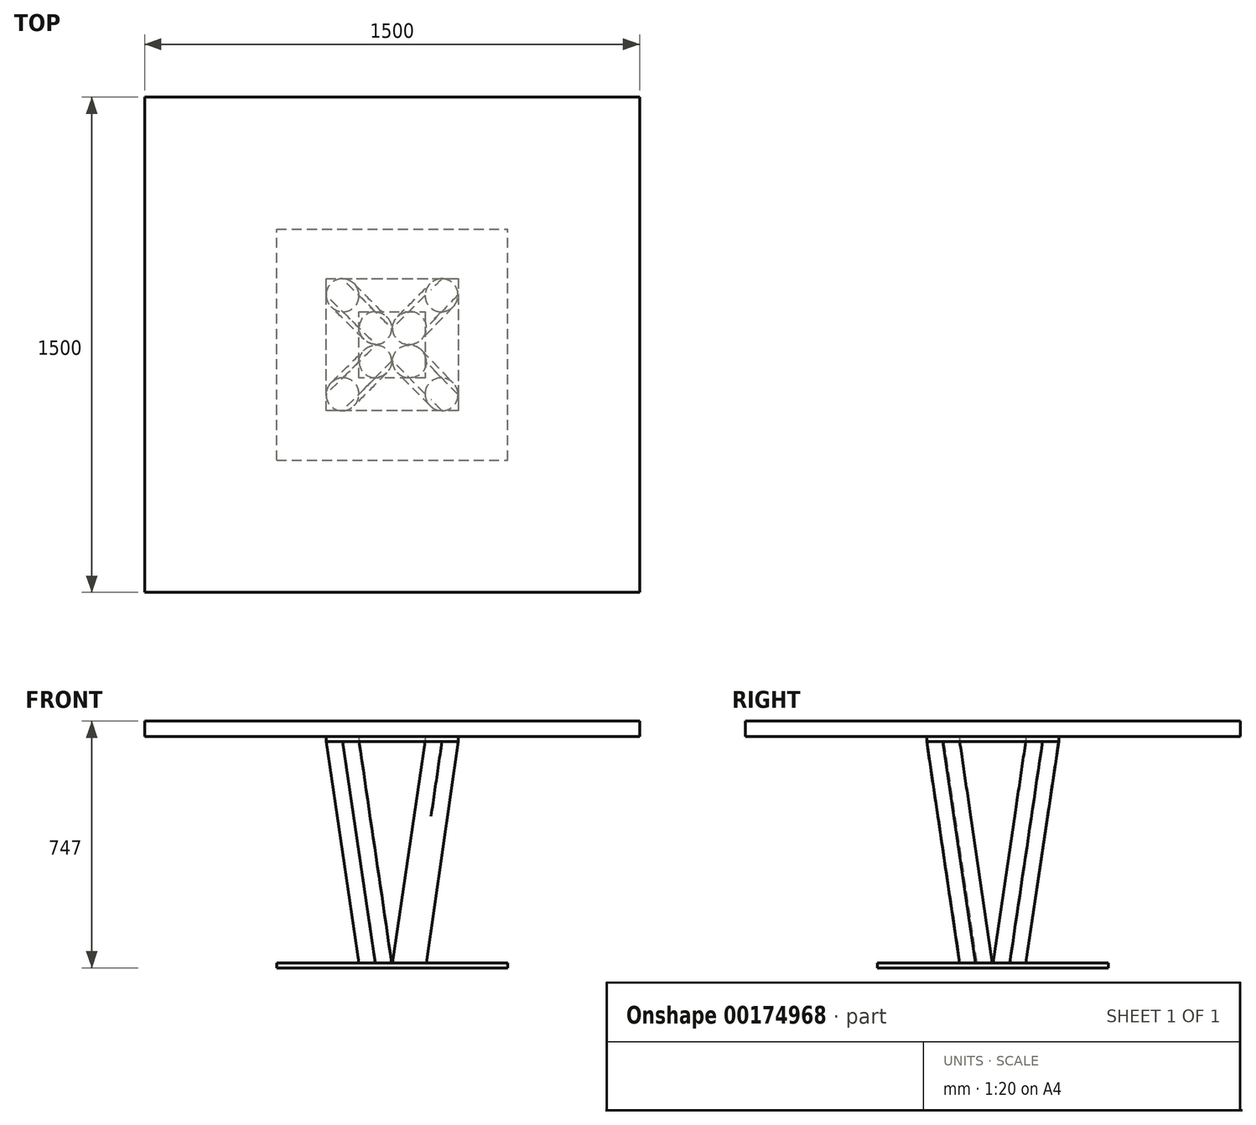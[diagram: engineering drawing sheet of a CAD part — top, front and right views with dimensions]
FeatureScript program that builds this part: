
annotation { "Feature Type Name" : "Feature", "Feature Type Description" : "" }
export const myFeature = defineFeature(function(context is Context, id is Id, definition is map)
    precondition{}
    {
        {
            var Q0;
            Q0=qCreatedBy(makeId("Front.planeOp"),FACE);
            var sketch = newSketch(context, id + "F0", { "sketchPlane" : qUnion([Q0])});
            skLineSegment(sketch, "E0.bottom", {"start": v(-350, -7.5) * mm, "end": v(350, -7.5) * mm});
            skLineSegment(sketch, "E0.top", {"start": v(-350, 7.5) * mm, "end": v(350, 7.5) * mm});
            skLineSegment(sketch, "E0.left", {"start": v(-350, -7.5) * mm, "end": v(-350, 7.5) * mm});
            skLineSegment(sketch, "E0.right", {"start": v(350, -7.5) * mm, "end": v(350, 7.5) * mm});
            skPoint(sketch, "E0.middle", {"position": v(0, 0) * mm});
            skSolve(sketch);
        }
        {
            var Q0;
            Q0 = qSketchRegion(id + "F0", true);
            extrude(context, id + "F1", {"entities" : qUnion([Q0]), "endBound" : BoundingType.SYMMETRIC, "depth" : 700 * mm});
        }
        {
            var Q0;
            Q0=makeQuery(id+"F1.opExtrude","SWEPT_FACE",FACE,{"disambiguationData":[OSD([sQuery(id+"F0.wireOp",EDGE,"E0.top")])]});
            var sketch = newSketch(context, id + "F2", { "sketchPlane" : qUnion([Q0])});
            skLineSegment(sketch, "E1.bottom", {"start": v(200, -200) * mm, "end": v(-200, -200) * mm});
            skLineSegment(sketch, "E1.top", {"start": v(200, 200) * mm, "end": v(-200, 200) * mm});
            skLineSegment(sketch, "E1.left", {"start": v(200, -200) * mm, "end": v(200, 200) * mm});
            skLineSegment(sketch, "E1.right", {"start": v(-200, -200) * mm, "end": v(-200, 200) * mm});
            skPoint(sketch, "E1.middle", {"position": v(0, 0) * mm});
            skSolve(sketch);
        }
        {
            var Q0;
            Q0=makeQuery(id+"F2.imprint","IMPRINT",FACE,{"disambiguationData":[TD([[makeQuery(id+"F2.imprint","IMPRINT",EDGE,{"derivedFrom":sQuery(id+"F2.wireOp",EDGE,"E1.bottom")}),-1.0]])]});
            extrude(context, id + "F3", {"entities" : qUnion([Q0]), "operationType" : NewBodyOperationType.ADD, "depth" : 670 * mm});
        }
        {
            var Q0;
            Q0=makeQuery(id+"F3.opExtrude","SWEPT_FACE",FACE,{"disambiguationData":[OSD([sQuery(id+"F2.wireOp",EDGE,"E1.right")])]});
            var sketch = newSketch(context, id + "F4", { "sketchPlane" : qUnion([Q0])});
            skLineSegment(sketch, "E2", {"start": v(200, 7.5) * mm, "end": v(200, 677.5) * mm});
            skLineSegment(sketch, "E3", {"start": v(200, 677.5) * mm, "end": v(100, 7.5) * mm});
            skLineSegment(sketch, "E4", {"start": v(100, 7.5) * mm, "end": v(200, 7.5) * mm});
            skLineSegment(sketch, "E5.MirrorCS", {"start": v(-200, 7.5) * mm, "end": v(-200, 677.5) * mm});
            skLineSegment(sketch, "E6.MirrorCS", {"start": v(-200, 677.5) * mm, "end": v(-100, 7.5) * mm});
            skLineSegment(sketch, "E7.MirrorCS", {"start": v(-100, 7.5) * mm, "end": v(-200, 7.5) * mm});
            skLineSegment(sketch, "E8", {"start": v(0, 0) * mm, "end": v(100, 677.5) * mm});
            skLineSegment(sketch, "E9", {"start": v(100, 677.5) * mm, "end": v(-100, 677.5) * mm});
            skLineSegment(sketch, "E10", {"start": v(-100, 677.5) * mm, "end": v(0, 0) * mm});
            skSolve(sketch);
        }
        {
            var Q0;
            Q0=makeQuery(id+"F3.opExtrude","SWEPT_FACE",FACE,{"disambiguationData":[OSD([sQuery(id+"F2.wireOp",EDGE,"E1.top")])]});
            var sketch = newSketch(context, id + "F5", { "sketchPlane" : qUnion([Q0])});
            skLineSegment(sketch, "E11", {"start": v(200, 7.5) * mm, "end": v(200, 677.5) * mm});
            skLineSegment(sketch, "E12", {"start": v(200, 677.5) * mm, "end": v(100, 7.5) * mm});
            skLineSegment(sketch, "E13", {"start": v(100, 7.5) * mm, "end": v(200, 7.5) * mm});
            skLineSegment(sketch, "E14.MirrorCS", {"start": v(-104.26, 7.5) * mm, "end": v(-200, 7.5) * mm});
            skLineSegment(sketch, "E15.MirrorCS", {"start": v(-100, 7.5) * mm, "end": v(-200, 7.5) * mm});
            skLineSegment(sketch, "E16.MirrorCS", {"start": v(-200, 677.5) * mm, "end": v(-104.26, 7.5) * mm});
            skLineSegment(sketch, "E17.MirrorCS", {"start": v(-200, 7.5) * mm, "end": v(-200, 677.5) * mm});
            skLineSegment(sketch, "E18", {"start": v(0, 0) * mm, "end": v(100, 677.5) * mm});
            skLineSegment(sketch, "E19", {"start": v(100, 677.5) * mm, "end": v(-100, 677.5) * mm});
            skLineSegment(sketch, "E20", {"start": v(-100, 677.5) * mm, "end": v(0, 0) * mm});
            skSolve(sketch);
        }
        {
            var Q0;
            Q0=makeQuery(id+"F5.imprint","IMPRINT",FACE,{"disambiguationData":[TD([[makeQuery(id+"F5.imprint","IMPRINT",EDGE,{"derivedFrom":sQuery(id+"F5.wireOp",EDGE,"E11")}),-1.0]])]});
            var Q1;
            {var subQ2=sQuery(id+"F5.wireOp",EDGE,"E16.MirrorCS");Q1=makeQuery(id+"F5.imprint","IMPRINT",FACE,{"disambiguationData":[TD([[makeQuery(id+"F5.imprint","IMPRINT",EDGE,{"derivedFrom":subQ2}),-1.0]])]});}
            extrude(context, id + "F6", {"entities" : qUnion([Q0, Q1]), "operationType" : NewBodyOperationType.REMOVE, "oppositeDirection" : true, "depth" : 2934.37 * mm});
        }
        {
            var Q0;
            Q0=makeQuery(id+"F4.imprint","IMPRINT",FACE,{"disambiguationData":[TD([[makeQuery(id+"F4.imprint","IMPRINT",EDGE,{"derivedFrom":sQuery(id+"F4.wireOp",EDGE,"E2")}),-1.0]])]});
            var Q1;
            Q1=makeQuery(id+"F4.imprint","IMPRINT",FACE,{"disambiguationData":[TD([[makeQuery(id+"F4.imprint","IMPRINT",EDGE,{"derivedFrom":sQuery(id+"F4.wireOp",EDGE,"E5.MirrorCS")}),1.0]])]});
            extrude(context, id + "F7", {"entities" : qUnion([Q0, Q1]), "operationType" : NewBodyOperationType.REMOVE, "oppositeDirection" : true, "depth" : 1558.7 * mm});
        }
        {
            var Q0;
            {var subQ0=sQuery(id+"F4.wireOp",EDGE,"E9");Q0=makeQuery(id+"F4.imprint","IMPRINT",FACE,{"disambiguationData":[TD([[makeQuery(id+"F4.imprint","IMPRINT",EDGE,{"derivedFrom":subQ0}),1.0]])]});}
            extrude(context, id + "F8", {"entities" : qUnion([Q0]), "operationType" : NewBodyOperationType.REMOVE, "oppositeDirection" : true, "depth" : 2927.5 * mm});
        }
        {
            var Q0;
            {var subQ0=sQuery(id+"F5.wireOp",EDGE,"E19");Q0=makeQuery(id+"F5.imprint","IMPRINT",FACE,{"disambiguationData":[TD([[makeQuery(id+"F5.imprint","IMPRINT",EDGE,{"derivedFrom":subQ0}),-1.0]])]});}
            extrude(context, id + "F9", {"entities" : qUnion([Q0]), "operationType" : NewBodyOperationType.REMOVE, "oppositeDirection" : true, "depth" : 814.42 * mm});
        }
        {
            var Q0;
            Q0=makeQuery(id+"F7.boolean.opBoolean","INTERSECT",EDGE,{"derivedFrom":[makeQuery(id+"F6.boolean.opBoolean","COPY",FACE,{"derivedFrom":makeQuery(id+"F6.opExtrude","SWEPT_FACE",FACE,{"disambiguationData":[OSD([sQuery(id+"F5.wireOp",EDGE,"E12")])]})}),makeQuery(id+"F7.opExtrude","SWEPT_FACE",FACE,{"disambiguationData":[OSD([sQuery(id+"F4.wireOp",EDGE,"E3")])]})]});
            fillet(context, id + "F10", {"entities" : qUnion([Q0]), "radius" : 50 * mm, "tangentPropagation" : true, "allowEdgeOverflow" : false});
        }
        {
            var Q0;
            Q0=makeQuery(id+"F8.boolean.opBoolean","INTERSECT",EDGE,{"derivedFrom":[makeQuery(id+"F6.boolean.opBoolean","COPY",FACE,{"derivedFrom":makeQuery(id+"F6.opExtrude","SWEPT_FACE",FACE,{"disambiguationData":[OSD([sQuery(id+"F5.wireOp",EDGE,"E12")])]})}),makeQuery(id+"F8.opExtrude","SWEPT_FACE",FACE,{"disambiguationData":[OSD([sQuery(id+"F4.wireOp",EDGE,"E8")])]})]});
            fillet(context, id + "F11", {"entities" : qUnion([Q0]), "radius" : 50 * mm, "tangentPropagation" : true, "allowEdgeOverflow" : false});
        }
        {
            var Q0;
            Q0=makeQuery(id+"F7.boolean.opBoolean","INTERSECT",EDGE,{"derivedFrom":[makeQuery(id+"F6.boolean.opBoolean","COPY",FACE,{"derivedFrom":makeQuery(id+"F6.opExtrude","SWEPT_FACE",FACE,{"disambiguationData":[OSD([sQuery(id+"F5.wireOp",EDGE,"E12")])]})}),makeQuery(id+"F7.opExtrude","SWEPT_FACE",FACE,{"disambiguationData":[OSD([sQuery(id+"F4.wireOp",EDGE,"E6.MirrorCS")])]})]});
            fillet(context, id + "F12", {"entities" : qUnion([Q0]), "radius" : 50 * mm, "tangentPropagation" : true, "allowEdgeOverflow" : false});
        }
        {
            var Q0;
            Q0=makeQuery(id+"F9.boolean.opBoolean","INTERSECT",EDGE,{"derivedFrom":[makeQuery(id+"F7.boolean.opBoolean","COPY",FACE,{"derivedFrom":makeQuery(id+"F7.opExtrude","SWEPT_FACE",FACE,{"disambiguationData":[OSD([sQuery(id+"F4.wireOp",EDGE,"E6.MirrorCS")])]})}),makeQuery(id+"F9.opExtrude","SWEPT_FACE",FACE,{"disambiguationData":[OSD([sQuery(id+"F5.wireOp",EDGE,"E18")])]})]});
            fillet(context, id + "F13", {"entities" : qUnion([Q0]), "radius" : 50 * mm, "tangentPropagation" : true, "allowEdgeOverflow" : false});
        }
        {
            var Q0;
            Q0=makeQuery(id+"F8.boolean.opBoolean","INTERSECT",EDGE,{"derivedFrom":[makeQuery(id+"F6.boolean.opBoolean","COPY",FACE,{"derivedFrom":makeQuery(id+"F6.opExtrude","SWEPT_FACE",FACE,{"disambiguationData":[OSD([sQuery(id+"F5.wireOp",EDGE,"E16.MirrorCS")])]})}),makeQuery(id+"F8.opExtrude","SWEPT_FACE",FACE,{"disambiguationData":[OSD([sQuery(id+"F4.wireOp",EDGE,"E10")])]})]});
            var Q1;
            Q1=makeQuery(id+"F7.boolean.opBoolean","INTERSECT",EDGE,{"derivedFrom":[makeQuery(id+"F6.boolean.opBoolean","COPY",FACE,{"derivedFrom":makeQuery(id+"F6.opExtrude","SWEPT_FACE",FACE,{"disambiguationData":[OSD([sQuery(id+"F5.wireOp",EDGE,"E16.MirrorCS")])]})}),makeQuery(id+"F7.opExtrude","SWEPT_FACE",FACE,{"disambiguationData":[OSD([sQuery(id+"F4.wireOp",EDGE,"E6.MirrorCS")])]})]});
            fillet(context, id + "F14", {"entities" : qUnion([Q0, Q1]), "radius" : 50 * mm, "tangentPropagation" : true, "allowEdgeOverflow" : false});
        }
        {
            var Q0;
            Q0=makeQuery(id+"F9.boolean.opBoolean","INTERSECT",EDGE,{"derivedFrom":[makeQuery(id+"F8.boolean.opBoolean","COPY",FACE,{"derivedFrom":makeQuery(id+"F8.opExtrude","SWEPT_FACE",FACE,{"disambiguationData":[OSD([sQuery(id+"F4.wireOp",EDGE,"E10")])]})}),makeQuery(id+"F9.opExtrude","SWEPT_FACE",FACE,{"disambiguationData":[OSD([sQuery(id+"F5.wireOp",EDGE,"E18")])]})]});
            var Q1;
            Q1=makeQuery(id+"F8.boolean.opBoolean","INTERSECT",EDGE,{"derivedFrom":[makeQuery(id+"F6.boolean.opBoolean","COPY",FACE,{"derivedFrom":makeQuery(id+"F6.opExtrude","SWEPT_FACE",FACE,{"disambiguationData":[OSD([sQuery(id+"F5.wireOp",EDGE,"E16.MirrorCS")])]})}),makeQuery(id+"F8.opExtrude","SWEPT_FACE",FACE,{"disambiguationData":[OSD([sQuery(id+"F4.wireOp",EDGE,"E8")])]})]});
            var Q2;
            Q2=makeQuery(id+"F9.boolean.opBoolean","INTERSECT",EDGE,{"derivedFrom":[makeQuery(id+"F7.boolean.opBoolean","COPY",FACE,{"derivedFrom":makeQuery(id+"F7.opExtrude","SWEPT_FACE",FACE,{"disambiguationData":[OSD([sQuery(id+"F4.wireOp",EDGE,"E3")])]})}),makeQuery(id+"F9.opExtrude","SWEPT_FACE",FACE,{"disambiguationData":[OSD([sQuery(id+"F5.wireOp",EDGE,"E18")])]})]});
            fillet(context, id + "F15", {"entities" : qUnion([Q0, Q1, Q2]), "radius" : 50 * mm, "tangentPropagation" : true, "allowEdgeOverflow" : false});
        }
        {
            var Q0;
            Q0=makeQuery(id+"F7.boolean.opBoolean","INTERSECT",EDGE,{"derivedFrom":[makeQuery(id+"F6.boolean.opBoolean","COPY",FACE,{"derivedFrom":makeQuery(id+"F6.opExtrude","SWEPT_FACE",FACE,{"disambiguationData":[OSD([sQuery(id+"F5.wireOp",EDGE,"E16.MirrorCS")])]})}),makeQuery(id+"F7.opExtrude","SWEPT_FACE",FACE,{"disambiguationData":[OSD([sQuery(id+"F4.wireOp",EDGE,"E3")])]})]});
            var Q1;
            Q1=makeQuery(id+"F9.boolean.opBoolean","INTERSECT",EDGE,{"derivedFrom":[makeQuery(id+"F7.boolean.opBoolean","COPY",FACE,{"derivedFrom":makeQuery(id+"F7.opExtrude","SWEPT_FACE",FACE,{"disambiguationData":[OSD([sQuery(id+"F4.wireOp",EDGE,"E3")])]})}),makeQuery(id+"F9.opExtrude","SWEPT_FACE",FACE,{"disambiguationData":[OSD([sQuery(id+"F5.wireOp",EDGE,"E20")])]})]});
            fillet(context, id + "F16", {"entities" : qUnion([Q0, Q1]), "radius" : 50 * mm, "tangentPropagation" : true, "allowEdgeOverflow" : false});
        }
        {
            var Q0;
            Q0=makeQuery(id+"F9.boolean.opBoolean","INTERSECT",EDGE,{"derivedFrom":[makeQuery(id+"F8.boolean.opBoolean","COPY",FACE,{"derivedFrom":makeQuery(id+"F8.opExtrude","SWEPT_FACE",FACE,{"disambiguationData":[OSD([sQuery(id+"F4.wireOp",EDGE,"E8")])]})}),makeQuery(id+"F9.opExtrude","SWEPT_FACE",FACE,{"disambiguationData":[OSD([sQuery(id+"F5.wireOp",EDGE,"E18")])]})]});
            fillet(context, id + "F17", {"entities" : qUnion([Q0]), "radius" : 50 * mm, "tangentPropagation" : true, "allowEdgeOverflow" : false});
        }
        {
            var Q0;
            Q0=makeQuery(id+"F9.boolean.opBoolean","INTERSECT",EDGE,{"derivedFrom":[makeQuery(id+"F8.boolean.opBoolean","COPY",FACE,{"derivedFrom":makeQuery(id+"F8.opExtrude","SWEPT_FACE",FACE,{"disambiguationData":[OSD([sQuery(id+"F4.wireOp",EDGE,"E8")])]})}),makeQuery(id+"F9.opExtrude","SWEPT_FACE",FACE,{"disambiguationData":[OSD([sQuery(id+"F5.wireOp",EDGE,"E20")])]})]});
            var Q1;
            Q1=makeQuery(id+"F8.boolean.opBoolean","INTERSECT",EDGE,{"derivedFrom":[makeQuery(id+"F6.boolean.opBoolean","COPY",FACE,{"derivedFrom":makeQuery(id+"F6.opExtrude","SWEPT_FACE",FACE,{"disambiguationData":[OSD([sQuery(id+"F5.wireOp",EDGE,"E12")])]})}),makeQuery(id+"F8.opExtrude","SWEPT_FACE",FACE,{"disambiguationData":[OSD([sQuery(id+"F4.wireOp",EDGE,"E10")])]})]});
            var Q2;
            Q2=makeQuery(id+"F9.boolean.opBoolean","INTERSECT",EDGE,{"derivedFrom":[makeQuery(id+"F8.boolean.opBoolean","COPY",FACE,{"derivedFrom":makeQuery(id+"F8.opExtrude","SWEPT_FACE",FACE,{"disambiguationData":[OSD([sQuery(id+"F4.wireOp",EDGE,"E10")])]})}),makeQuery(id+"F9.opExtrude","SWEPT_FACE",FACE,{"disambiguationData":[OSD([sQuery(id+"F5.wireOp",EDGE,"E20")])]})]});
            fillet(context, id + "F18", {"entities" : qUnion([Q0, Q1, Q2]), "radius" : 50 * mm, "tangentPropagation" : true, "allowEdgeOverflow" : false});
        }
        {
            var Q0;
            Q0=makeQuery(id+"F9.boolean.opBoolean","INTERSECT",EDGE,{"derivedFrom":[makeQuery(id+"F7.boolean.opBoolean","COPY",FACE,{"derivedFrom":makeQuery(id+"F7.opExtrude","SWEPT_FACE",FACE,{"disambiguationData":[OSD([sQuery(id+"F4.wireOp",EDGE,"E6.MirrorCS")])]})}),makeQuery(id+"F9.opExtrude","SWEPT_FACE",FACE,{"disambiguationData":[OSD([sQuery(id+"F5.wireOp",EDGE,"E20")])]})]});
            fillet(context, id + "F19", {"entities" : qUnion([Q0]), "radius" : 50 * mm, "tangentPropagation" : true, "allowEdgeOverflow" : false});
        }
        {
            var Q0;
            {var subQ0=makeQuery(id+"F6.boolean.opBoolean","COPY",FACE,{"derivedFrom":makeQuery(id+"F6.opExtrude","SWEPT_FACE",FACE,{"disambiguationData":[OSD([sQuery(id+"F5.wireOp",EDGE,"E16.MirrorCS")])]})});var subQ1=makeQuery(id+"F7.boolean.opBoolean","COPY",FACE,{"derivedFrom":makeQuery(id+"F7.opExtrude","SWEPT_FACE",FACE,{"disambiguationData":[OSD([sQuery(id+"F4.wireOp",EDGE,"E6.MirrorCS")])]})});Q0=makeQuery(id+"F9.boolean.opBoolean","SPLIT",FACE,{"disambiguationData":[TD([subQ0])],"derivedFrom":makeQuery(id+"F8.boolean.opBoolean","SPLIT",FACE,{"disambiguationData":[TD([subQ1])],"derivedFrom":makeQuery(id+"F3.opExtrude","CAP_FACE",FACE,{"disambiguationData":[OSD([sQuery(id+"F2.wireOp",EDGE,"E1.bottom"),sQuery(id+"F2.wireOp",EDGE,"E1.top"),sQuery(id+"F2.wireOp",EDGE,"E1.left"),sQuery(id+"F2.wireOp",EDGE,"E1.right")])],"isStart":false})})});}
            var sketch = newSketch(context, id + "F20", { "sketchPlane" : qUnion([Q0])});
            skLineSegment(sketch, "E21", {"start": v(200, 200) * mm, "end": v(200, -200) * mm});
            skLineSegment(sketch, "E22", {"start": v(200, -200) * mm, "end": v(-200, -200) * mm});
            skLineSegment(sketch, "E23", {"start": v(-200, -200) * mm, "end": v(-200, 200) * mm});
            skLineSegment(sketch, "E24", {"start": v(-200, 200) * mm, "end": v(200, 200) * mm});
            skLineSegment(sketch, "E25.0", {"start": v(100, 100) * mm, "end": v(100, -100) * mm});
            skLineSegment(sketch, "E25.1", {"start": v(-100, 100) * mm, "end": v(100, 100) * mm});
            skLineSegment(sketch, "E25.2", {"start": v(-100, -100) * mm, "end": v(-100, 100) * mm});
            skLineSegment(sketch, "E25.3", {"start": v(100, -100) * mm, "end": v(-100, -100) * mm});
            skSolve(sketch);
        }
        {
            var Q0;
            {var subQ0=makeQuery(id+"F6.boolean.opBoolean","COPY",FACE,{"derivedFrom":makeQuery(id+"F6.opExtrude","SWEPT_FACE",FACE,{"disambiguationData":[OSD([sQuery(id+"F5.wireOp",EDGE,"E16.MirrorCS")])]})});var subQ1=makeQuery(id+"F7.opExtrude","SWEPT_FACE",FACE,{"disambiguationData":[OSD([sQuery(id+"F4.wireOp",EDGE,"E6.MirrorCS")])]});var subQ2=makeQuery(id+"F7.boolean.opBoolean","COPY",FACE,{"derivedFrom":subQ1});var subQ3=makeQuery(id+"F8.opExtrude","SWEPT_FACE",FACE,{"disambiguationData":[OSD([sQuery(id+"F4.wireOp",EDGE,"E10")])]});var subQ4=makeQuery(id+"F8.boolean.opBoolean","COPY",FACE,{"derivedFrom":subQ3});var subQ5=makeQuery(id+"F9.opExtrude","SWEPT_FACE",FACE,{"disambiguationData":[OSD([sQuery(id+"F5.wireOp",EDGE,"E20")])]});var subQ6=makeQuery(id+"F9.boolean.opBoolean","SPLIT",FACE,{"disambiguationData":[TD([subQ0])],"derivedFrom":makeQuery(id+"F8.boolean.opBoolean","SPLIT",FACE,{"disambiguationData":[TD([subQ2])],"derivedFrom":makeQuery(id+"F3.opExtrude","CAP_FACE",FACE,{"disambiguationData":[OSD([sQuery(id+"F2.wireOp",EDGE,"E1.bottom"),sQuery(id+"F2.wireOp",EDGE,"E1.top"),sQuery(id+"F2.wireOp",EDGE,"E1.left"),sQuery(id+"F2.wireOp",EDGE,"E1.right")])],"isStart":false})})});var subQ7=subQ6;Q0=makeQuery(id+"F20.imprint","IMPRINT",FACE,{"disambiguationData":[TD([[makeQuery(id+"F20.imprint","IMPRINT",EDGE,{"derivedFrom":makeQuery(id+"F18.opFillet","BLEND_EDGE",EDGE,{"blendedFrom":[makeQuery(id+"F9.boolean.opBoolean","INTERSECT",EDGE,{"derivedFrom":[subQ4,subQ5]}),subQ7],"blendedInto":[subQ7]})}),1.0]])]});}
            var Q1;
            {var subQ1=makeQuery(id+"F6.boolean.opBoolean","COPY",FACE,{"derivedFrom":makeQuery(id+"F6.opExtrude","SWEPT_FACE",FACE,{"disambiguationData":[OSD([sQuery(id+"F5.wireOp",EDGE,"E16.MirrorCS")])]})});var subQ2=makeQuery(id+"F7.opExtrude","SWEPT_FACE",FACE,{"disambiguationData":[OSD([sQuery(id+"F4.wireOp",EDGE,"E6.MirrorCS")])]});var subQ3=makeQuery(id+"F7.boolean.opBoolean","COPY",FACE,{"derivedFrom":subQ2});var subQ6=makeQuery(id+"F9.boolean.opBoolean","SPLIT",FACE,{"disambiguationData":[TD([subQ1])],"derivedFrom":makeQuery(id+"F8.boolean.opBoolean","SPLIT",FACE,{"disambiguationData":[TD([subQ3])],"derivedFrom":makeQuery(id+"F3.opExtrude","CAP_FACE",FACE,{"disambiguationData":[OSD([sQuery(id+"F2.wireOp",EDGE,"E1.bottom"),sQuery(id+"F2.wireOp",EDGE,"E1.top"),sQuery(id+"F2.wireOp",EDGE,"E1.left"),sQuery(id+"F2.wireOp",EDGE,"E1.right")])],"isStart":false})})});var subQ7=makeQuery(id+"F14.opFillet","BLEND_EDGE",EDGE,{"blendedFrom":[makeQuery(id+"F7.boolean.opBoolean","INTERSECT",EDGE,{"derivedFrom":[subQ1,subQ2]}),subQ6],"blendedInto":[subQ6]});Q1=makeQuery(id+"F20.imprint","IMPRINT",FACE,{"disambiguationData":[TD([[makeQuery(id+"F20.imprint","IMPRINT",EDGE,{"derivedFrom":subQ7}),-1.0]])]});}
            var Q2;
            {var subQ10=sQuery(id+"F20.wireOp",EDGE,"E22");Q2=makeQuery(id+"F20.imprint","IMPRINT",FACE,{"disambiguationData":[TD([[makeQuery(id+"F20.imprint","IMPRINT",EDGE,{"derivedFrom":subQ10}),-1.0]])]});}
            extrude(context, id + "F21", {"entities" : qUnion([Q0, Q1, Q2]), "operationType" : NewBodyOperationType.ADD, "depth" : 15 * mm});
        }
        {
            var Q0;
            Q0=makeQuery(id+"F21.opExtrude","CAP_FACE",FACE,{"disambiguationData":[OSD([sQuery(id+"F20.wireOp",EDGE,"E21"),sQuery(id+"F20.wireOp",EDGE,"E22"),sQuery(id+"F20.wireOp",EDGE,"E23"),sQuery(id+"F20.wireOp",EDGE,"E24"),sQuery(id+"F20.wireOp",EDGE,"E25.0"),sQuery(id+"F20.wireOp",EDGE,"E25.1"),sQuery(id+"F20.wireOp",EDGE,"E25.2"),sQuery(id+"F20.wireOp",EDGE,"E25.3")])],"isStart":false});
            var sketch = newSketch(context, id + "F22", { "sketchPlane" : qUnion([Q0])});
            skLineSegment(sketch, "E26.bottom", {"start": v(750, 750) * mm, "end": v(-750, 750) * mm});
            skLineSegment(sketch, "E26.top", {"start": v(750, -750) * mm, "end": v(-750, -750) * mm});
            skLineSegment(sketch, "E26.left", {"start": v(750, 750) * mm, "end": v(750, -750) * mm});
            skLineSegment(sketch, "E26.right", {"start": v(-750, 750) * mm, "end": v(-750, -750) * mm});
            skPoint(sketch, "E26.middle", {"position": v(0, 0) * mm});
            skSolve(sketch);
        }
        {
            var Q0;
            Q0=makeQuery(id+"F22.imprint","IMPRINT",FACE,{"disambiguationData":[TD([[makeQuery(id+"F22.imprint","IMPRINT",EDGE,{"derivedFrom":makeQuery(id+"F21.opExtrude","CAP_EDGE",EDGE,{"disambiguationData":[OSD([sQuery(id+"F20.wireOp",EDGE,"E25.0")])],"isStart":false})}),-1.0]])]});
            var Q1;
            Q1=makeQuery(id+"F22.imprint","IMPRINT",FACE,{"disambiguationData":[TD([[makeQuery(id+"F22.imprint","IMPRINT",EDGE,{"derivedFrom":sQuery(id+"F22.wireOp",EDGE,"E26.bottom")}),1.0]])]});
            var Q2;
            Q2=makeQuery(id+"F22.imprint","IMPRINT",FACE,{"disambiguationData":[TD([[makeQuery(id+"F22.imprint","IMPRINT",EDGE,{"derivedFrom":makeQuery(id+"F21.opExtrude","CAP_EDGE",EDGE,{"disambiguationData":[OSD([sQuery(id+"F20.wireOp",EDGE,"E21")])],"isStart":false})}),-1.0]])]});
            extrude(context, id + "F23", {"entities" : qUnion([Q0, Q1, Q2]), "operationType" : NewBodyOperationType.ADD, "depth" : 47 * mm});
        }
    });
